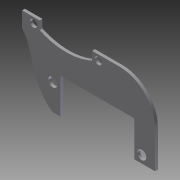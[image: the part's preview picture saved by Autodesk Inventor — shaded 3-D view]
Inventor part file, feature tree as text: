
AUTODESK INVENTOR PART (.ipt)
format: ipt  version: 2012 (Build 160160000, 160)  size: 122,880 bytes
history: native  units: in
note: dims shown in document units (in); Inventor stores cm internally (conversion verified against a paired STEP export)
features: extrude x1, fillet x1, sketch x1
ambient origin geometry x8: Origin, YZ Plane, XZ Plane, XY Plane, X Axis, Y Axis, Z Axis, Center Point
bodies: Solid1 (feature_tree)
feature tree (3):
  extrude  "Extrusion1"  Depth=1.54in
  fillet  "Fillet1"  Radius=0.44in
  sketch  "Sketch1"  dims[d0=2.81in d1=1.54in d2=0.44in d3=2.0in d4=0.75in d5=2.56in d6=1.88in d7=1.33in d8=2.44in d9=1.32in d10=0.192in d11=0.192in d12=0.28in d13=0.16in d14=2.16in d15=0.55in d16=0.15in d17=0.15in d18=1.42in d19=1.2in d20=2.57in d21=0.325in d22=0.06in d23=0.0in d24=0.75in]
